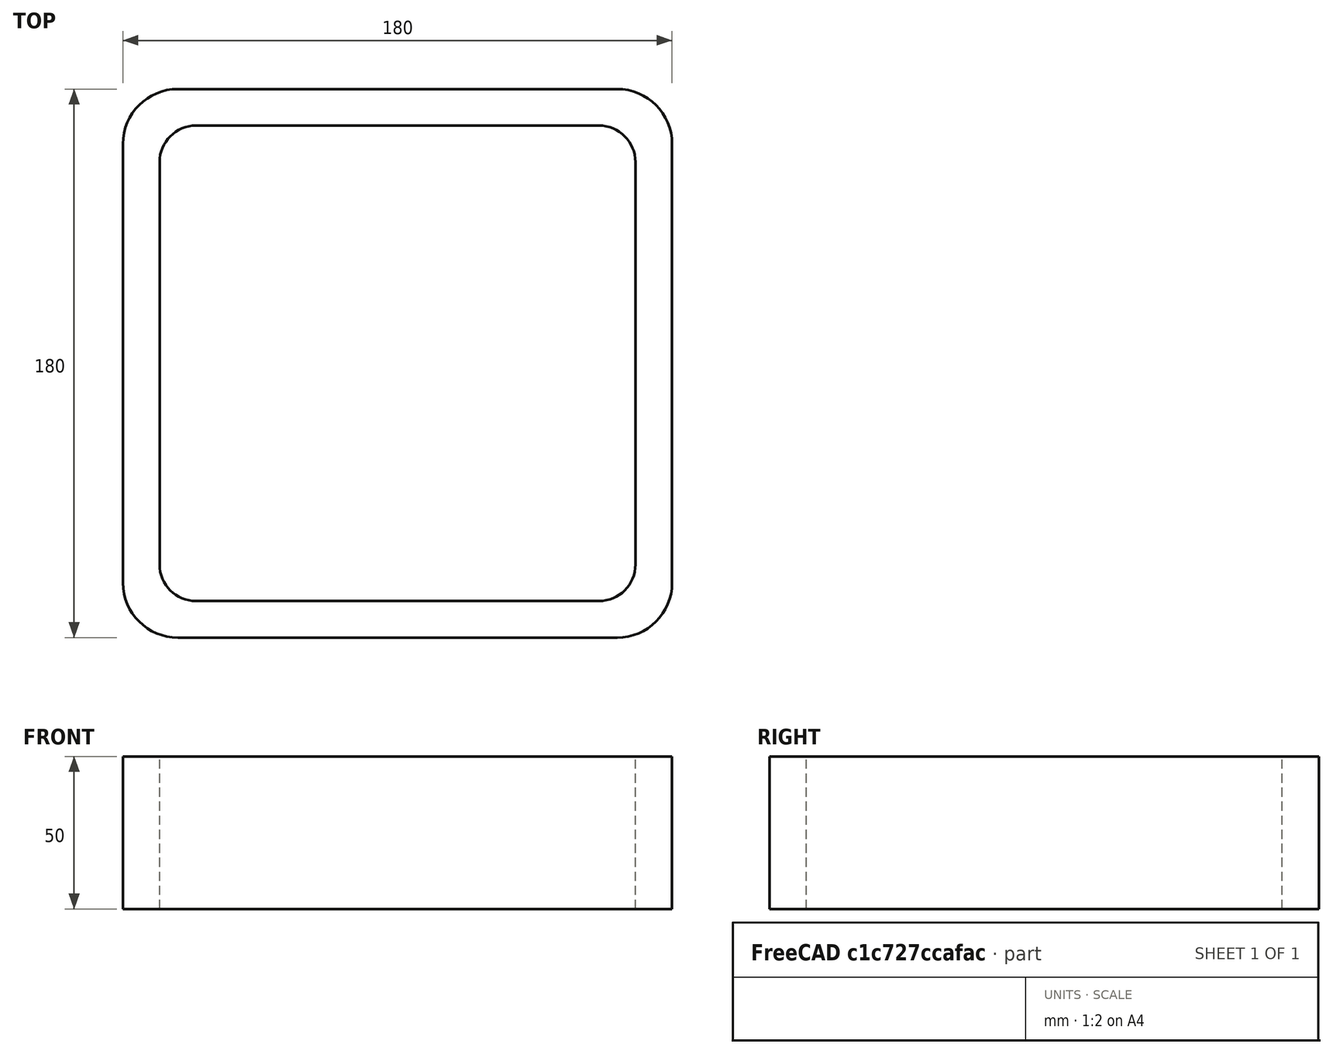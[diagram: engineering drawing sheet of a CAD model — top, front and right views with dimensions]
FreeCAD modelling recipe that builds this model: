
FCSTD DOCUMENT  (FreeCAD 0.15R4671 (Git))
Label: Square hollow section 180x180x12 EN10219 S235JRH
License: All rights reserved
LicenseURL: http://en.wikipedia.org/wiki/All_rights_reserved
objects: Sketcher::SketchObject×1, Part::Extrusion×1
note: 2 computed .brp shape members not serialized (recipe doc carries the construction recipe); baked Part::Feature solids carry a one-line shape summary decoded from their .brp

FEATURE [Sketcher::SketchObject] Sketch
  sketch-geometry (16):
    g0: LineSegment StartX=-66 StartY=78 StartZ=0 EndX=66 EndY=78 EndZ=0
    g1: LineSegment StartX=78 StartY=66 StartZ=0 EndX=78 EndY=-66 EndZ=0
    g2: LineSegment StartX=66 StartY=-78 StartZ=0 EndX=-66 EndY=-78 EndZ=0
    g3: LineSegment StartX=-78 StartY=-66 StartZ=0 EndX=-78 EndY=66 EndZ=0
    g4: LineSegment StartX=-72 StartY=90 StartZ=0 EndX=72 EndY=90 EndZ=0
    g5: LineSegment StartX=90 StartY=72 StartZ=0 EndX=90 EndY=-72 EndZ=0
    g6: LineSegment StartX=72 StartY=-90 StartZ=0 EndX=-72 EndY=-90 EndZ=0
    g7: LineSegment StartX=-90 StartY=-72 StartZ=0 EndX=-90 EndY=72 EndZ=0
    g8: ArcOfCircle CenterX=-66 CenterY=66 CenterZ=0 NormalX=0 NormalY=0 NormalZ=1 Radius=12 StartAngle=1.5708 EndAngle=3.14159
    g9: ArcOfCircle CenterX=66 CenterY=66 CenterZ=0 NormalX=0 NormalY=0 NormalZ=1 Radius=12 StartAngle=0 EndAngle=1.5708
    g10: ArcOfCircle CenterX=66 CenterY=-66 CenterZ=0 NormalX=0 NormalY=0 NormalZ=1 Radius=12 StartAngle=4.71239 EndAngle=6.28319
    g11: ArcOfCircle CenterX=-66 CenterY=-66 CenterZ=0 NormalX=0 NormalY=0 NormalZ=1 Radius=12 StartAngle=3.14159 EndAngle=4.71239
    g12: ArcOfCircle CenterX=72 CenterY=72 CenterZ=0 NormalX=0 NormalY=0 NormalZ=1 Radius=18 StartAngle=0 EndAngle=1.5708
    g13: ArcOfCircle CenterX=72 CenterY=-72 CenterZ=0 NormalX=0 NormalY=0 NormalZ=1 Radius=18 StartAngle=4.71239 EndAngle=6.28319
    g14: ArcOfCircle CenterX=-72 CenterY=-72 CenterZ=0 NormalX=0 NormalY=0 NormalZ=1 Radius=18 StartAngle=3.14159 EndAngle=4.71239
    g15: ArcOfCircle CenterX=-72 CenterY=72 CenterZ=0 NormalX=0 NormalY=0 NormalZ=1 Radius=18 StartAngle=1.5708 EndAngle=3.14159
  constraints (36):
    c: Horizontal(g2)
    c: Vertical(g3)
    c: Horizontal(g6)
    c: Vertical(g7)
    c: Tangent(g3,g8) = 1.5708
    c: Tangent(g0,g8) = 1.5708
    c: Tangent(g0,g9) = 1.5708
    c: Tangent(g1,g9) = 1.5708
    c: Tangent(g1,g10) = 1.5708
    c: Tangent(g2,g10) = 1.5708
    c: Tangent(g2,g11) = 1.5708
    c: Tangent(g3,g11) = 1.5708
    c: Tangent(g4,g12) = 1.5708
    c: Tangent(g5,g12) = 1.5708
    c: Tangent(g5,g13) = 1.5708
    c: Tangent(g6,g13) = 1.5708
    c: Tangent(g6,g14) = 1.5708
    c: Tangent(g7,g14) = 1.5708
    c: Tangent(g7,g15) = 1.5708
    c: Tangent(g4,g15) = 1.5708
    c: Equal(g9,g8)
    c: Equal(g9,g11)
    c: Equal(g9,g10)
    c: Equal(g12,g15)
    c: Equal(g12,g14)
    c: Equal(g12,g13)
    c: Symmetric(g4,g6,g-1)
    c: Symmetric(g7,g5,g-2)
    c: DistanceY(g4,g6) = -180
    c: DistanceX(g7,g5) = 180
    c: Symmetric(g3,g1,g-2)
    c: Symmetric(g0,g2,g-1)
    c: DistanceY(g0,g4) = 12
    c: DistanceX(g5,g1) = -12
    c: Radius(g9) = 12
    c: Radius(g12) = 18
FEATURE [Part::Extrusion] Extrude  label="Square hollow section 180x180x12 EN10219 S235JRH"
  Base = -> Sketch
  Dir = (0,0,50)
  Solid = true
